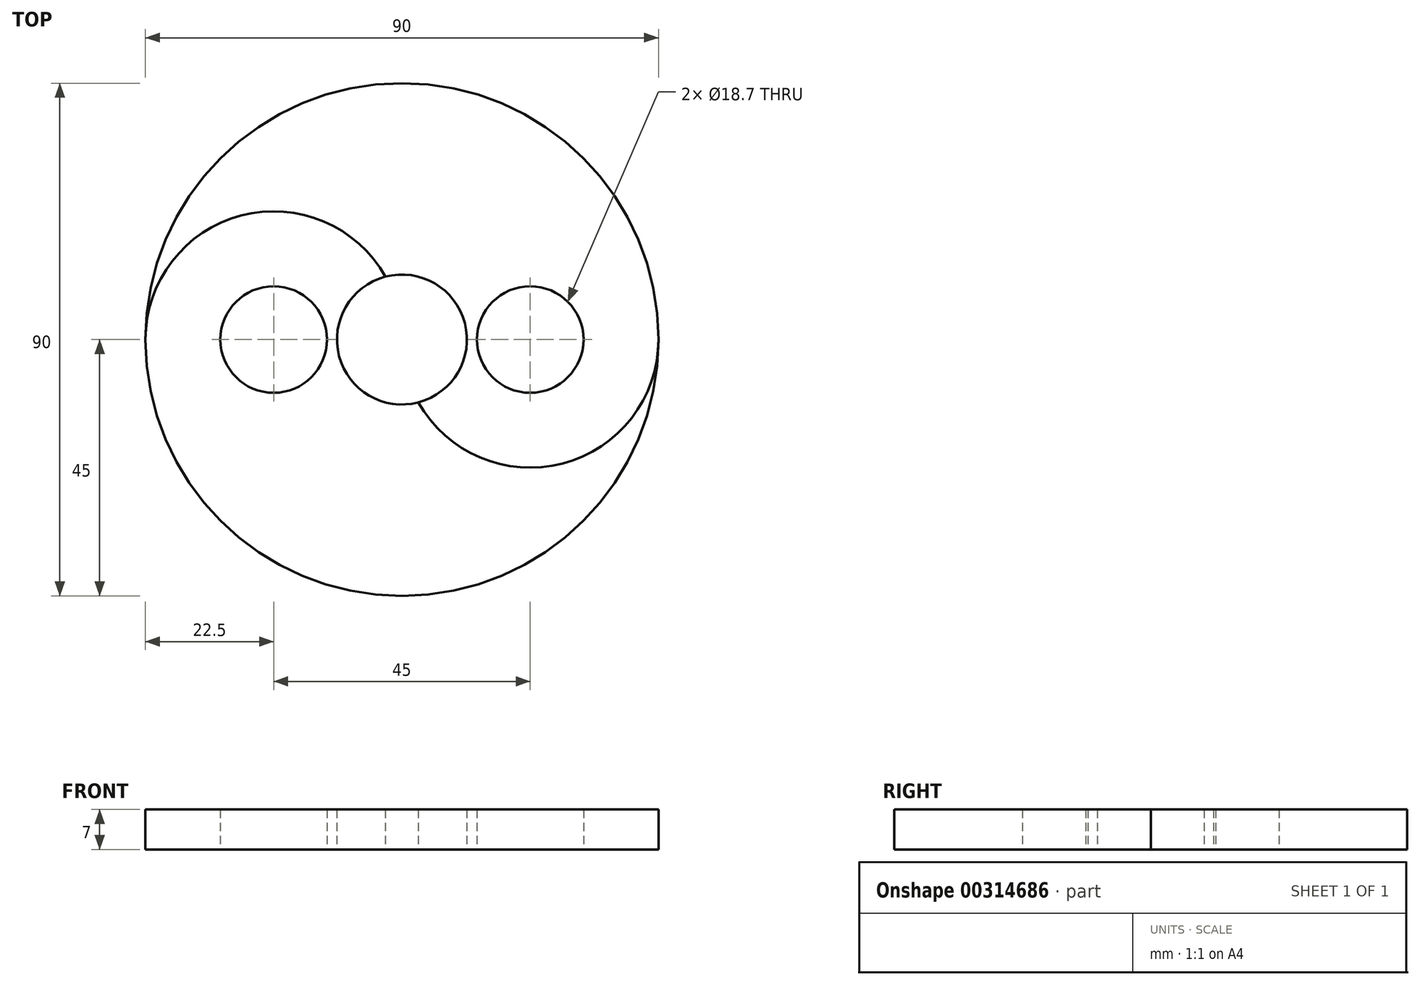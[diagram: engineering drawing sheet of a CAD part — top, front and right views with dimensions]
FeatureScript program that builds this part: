
annotation { "Feature Type Name" : "Feature", "Feature Type Description" : "" }
export const myFeature = defineFeature(function(context is Context, id is Id, definition is map)
    precondition{}
    {
        {
            var Q0;
            Q0=qCreatedBy(makeId("Top.planeOp"),FACE);
            var sketch = newSketch(context, id + "F0", { "sketchPlane" : qUnion([Q0])});
            skCircle(sketch, "E0", {"center": v(0, 0) * mm, "radius": 45 * mm});
            skLineSegment(sketch, "E1", {"start": v(0, 45) * mm, "end": v(0, -45) * mm, "construction": true});
            skLineSegment(sketch, "E2", {"start": v(-45, 0) * mm, "end": v(45, 0) * mm, "construction": true});
            skCircle(sketch, "E3", {"center": v(0, 0) * mm, "radius": 11.4 * mm});
            skArc(sketch, "E4", {"start": v(0, 0) * mm, "mid": v(-22.5, 22.5) * mm, "end": v(-45, 0) * mm});
            skArc(sketch, "E5", {"start": v(0, 0) * mm, "mid": v(22.5, -22.5) * mm, "end": v(45, 0) * mm});
            skCircle(sketch, "E6", {"center": v(-22.5, 0) * mm, "radius": 9.35 * mm});
            skCircle(sketch, "E7", {"center": v(22.5, 0) * mm, "radius": 9.35 * mm});
            skSolve(sketch);
        }
        {
            var Q0;
            Q0=makeQuery(id+"F0.imprint","IMPRINT",FACE,{"disambiguationData":[TD([[makeQuery(id+"F0.imprint","IMPRINT",EDGE,{"derivedFrom":sQuery(id+"F0.wireOp",EDGE,"E6")}),-1.0]])]});
            extrude(context, id + "F1", {"entities" : qUnion([Q0]), "depth" : 7 * mm, "offsetDistance" : 25 * mm});
        }
        {
            var Q0;
            Q0=makeQuery(id+"F0.imprint","IMPRINT",FACE,{"disambiguationData":[TD([[makeQuery(id+"F0.imprint","IMPRINT",EDGE,{"derivedFrom":sQuery(id+"F0.wireOp",EDGE,"E7")}),-1.0]])]});
            extrude(context, id + "F2", {"entities" : qUnion([Q0]), "depth" : 7 * mm, "offsetDistance" : 25 * mm});
        }
    });
